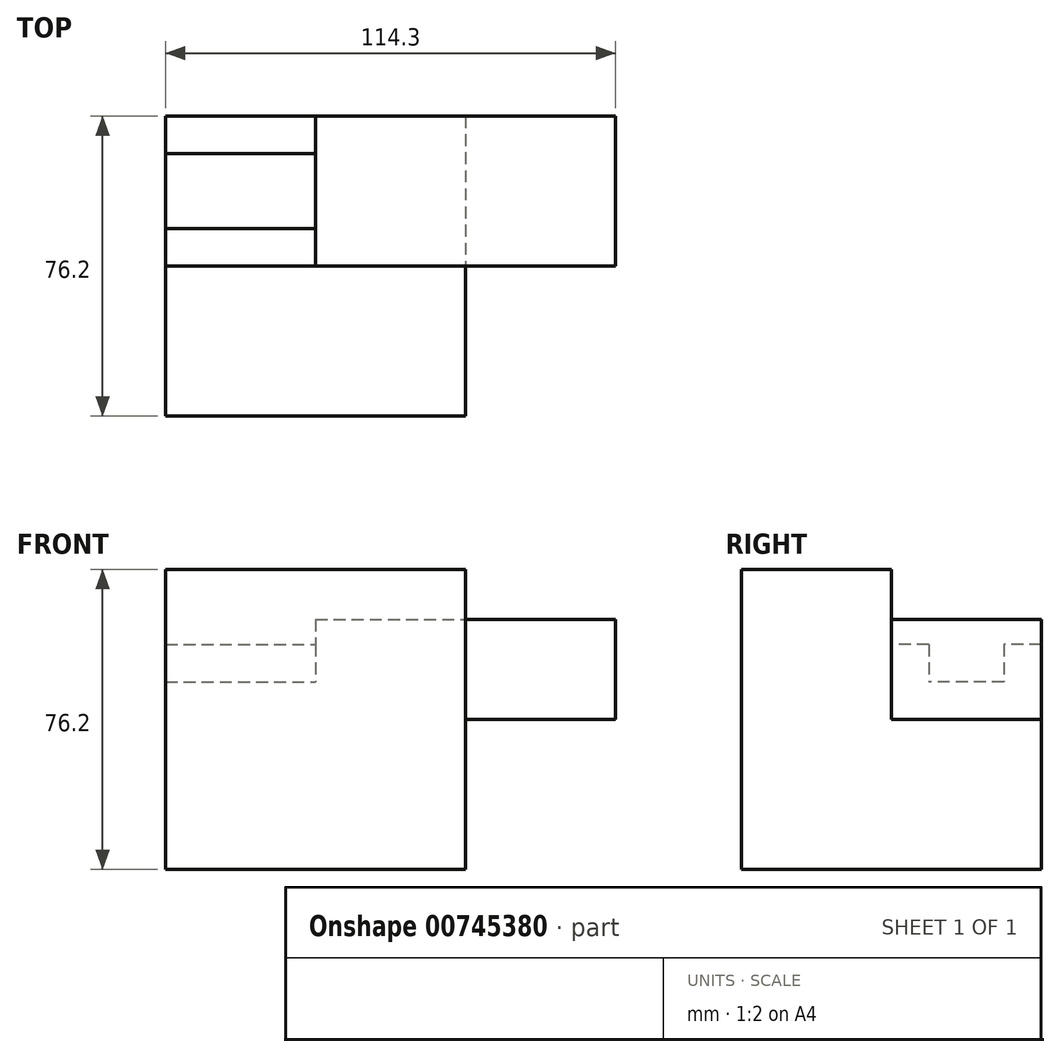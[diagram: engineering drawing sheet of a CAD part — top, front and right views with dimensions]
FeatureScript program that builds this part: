
annotation { "Feature Type Name" : "Feature", "Feature Type Description" : "" }
export const myFeature = defineFeature(function(context is Context, id is Id, definition is map)
    precondition{}
    {
        {
            var Q0;
            Q0=qCreatedBy(makeId("Top.planeOp"),FACE);
            var sketch = newSketch(context, id + "F0", { "sketchPlane" : qUnion([Q0])});
            skLineSegment(sketch, "E0.bottom", {"start": v(38.1, 38.1) * mm, "end": v(-38.1, 38.1) * mm});
            skLineSegment(sketch, "E0.top", {"start": v(38.1, -38.1) * mm, "end": v(-38.1, -38.1) * mm});
            skLineSegment(sketch, "E0.left", {"start": v(38.1, 38.1) * mm, "end": v(38.1, -38.1) * mm});
            skLineSegment(sketch, "E0.right", {"start": v(-38.1, 38.1) * mm, "end": v(-38.1, -38.1) * mm});
            skPoint(sketch, "E0.middle", {"position": v(0, 0) * mm});
            skSolve(sketch);
        }
        {
            var Q0;
            Q0 = qSketchRegion(id + "F0", true);
            extrude(context, id + "F1", {"entities" : qUnion([Q0]), "endBound" : BoundingType.SYMMETRIC, "depth" : 76.2 * mm, "offsetDistance" : 25.4 * mm});
        }
        {
            var Q0;
            Q0=qCreatedBy(makeId("Right.planeOp"),FACE);
            var sketch = newSketch(context, id + "F2", { "sketchPlane" : qUnion([Q0])});
            skLineSegment(sketch, "E1.bottom", {"start": v(28.57, 28.58) * mm, "end": v(9.52, 28.58) * mm});
            skLineSegment(sketch, "E1.top", {"start": v(28.58, 9.53) * mm, "end": v(9.53, 9.52) * mm});
            skLineSegment(sketch, "E1.left", {"start": v(28.57, 28.58) * mm, "end": v(28.58, 9.53) * mm});
            skLineSegment(sketch, "E1.right", {"start": v(9.52, 28.57) * mm, "end": v(9.53, 9.53) * mm});
            skPoint(sketch, "E1.middle", {"position": v(19.05, 19.05) * mm});
            skSolve(sketch);
        }
        {
            var Q0;
            Q0 = qSketchRegion(id + "F2", true);
            extrude(context, id + "F3", {"entities" : qUnion([Q0]), "operationType" : NewBodyOperationType.REMOVE, "oppositeDirection" : true, "depth" : 38.1 * mm, "offsetDistance" : 25.4 * mm});
        }
        {
            var Q0;
            Q0=makeQuery(id+"F1.opExtrude","CAP_FACE",FACE,{"disambiguationData":[OSD([sQuery(id+"F0.wireOp",EDGE,"E0.bottom"),sQuery(id+"F0.wireOp",EDGE,"E0.top"),sQuery(id+"F0.wireOp",EDGE,"E0.left"),sQuery(id+"F0.wireOp",EDGE,"E0.right")])],"isStart":false});
            var sketch = newSketch(context, id + "F4", { "sketchPlane" : qUnion([Q0])});
            skLineSegment(sketch, "E2.bottom", {"start": v(-38.1, 0) * mm, "end": v(38.1, 0) * mm});
            skLineSegment(sketch, "E2.top", {"start": v(-38.1, 38.1) * mm, "end": v(38.1, 38.1) * mm});
            skLineSegment(sketch, "E2.left", {"start": v(-38.1, 0) * mm, "end": v(-38.1, 38.1) * mm});
            skLineSegment(sketch, "E2.right", {"start": v(38.1, 0) * mm, "end": v(38.1, 38.1) * mm});
            skSolve(sketch);
        }
        {
            var Q0;
            Q0 = qSketchRegion(id + "F4", true);
            extrude(context, id + "F5", {"entities" : qUnion([Q0]), "operationType" : NewBodyOperationType.REMOVE, "oppositeDirection" : true, "depth" : 19.05 * mm, "offsetDistance" : 25.4 * mm});
        }
        {
            var Q0;
            Q0=qCreatedBy(makeId("Top.planeOp"),FACE);
            var sketch = newSketch(context, id + "F6", { "sketchPlane" : qUnion([Q0])});
            skLineSegment(sketch, "E3.bottom", {"start": v(0, 0) * mm, "end": v(76.2, 0) * mm});
            skLineSegment(sketch, "E3.top", {"start": v(0, 38.1) * mm, "end": v(76.2, 38.1) * mm});
            skLineSegment(sketch, "E3.left", {"start": v(0, 0) * mm, "end": v(0, 38.1) * mm});
            skLineSegment(sketch, "E3.right", {"start": v(76.2, 0) * mm, "end": v(76.2, 38.1) * mm});
            skSolve(sketch);
        }
        {
            var Q0;
            Q0 = qSketchRegion(id + "F6", true);
            extrude(context, id + "F7", {"entities" : qUnion([Q0]), "operationType" : NewBodyOperationType.ADD, "depth" : 25.4 * mm, "offsetDistance" : 25.4 * mm});
        }
    });
